# Revit family: MAD-412-I_Módulo analógico 2 salidas relé
name_source: partatom
category: Dispositivos de alarma de incendios
revit_build: Autodesk Revit 2017 (Build: 20190508_0315(x64)
units: mm (PartAtom-declared; Revit-internal decimal feet)

## family parameters
Anfitrión = Cara
Compartido = No
Corte con vacíos al cargar = No
Cota de conector redondo = Diámetro de uso
Mantener orientación de anotación = No
Punto de cálculo de habitación = No
Tipo de pieza = Normal

## types (1)
- MAD-412-I
    Altura = 100 mm
    Anchura = 100 mm
    Carga eléctrica = Otro
    Certificación = EN 54-18 y EN 54-17
    Comentarios de tipo = Los módulos son idóneos para la activación o paro de cualquier dispositivo. También son idóneos para interrelacionar sistemas donde las entradas de dichos sistemas admitan contactos libres de potencial, por ejemplo, el paro de la ventilación, el paro de los ascensores o la activación de los exutorios.
    Conexionado = 2 x 1,5 mm² trenzado y apantallado
    Consumo en alarma = < 3 mA
    Consumo en reposo = < 300 μA
    Cuerpo = ABS Rojo
    Código de montaje = PDETMAD-412-I
    Descripción = Módulo analógico de control con aislador incorporado de 2 salidas de relé libre de tensión que proporciona dos contactos C, NA, NC no reseteable. Marca Detnov, modelo MAD-412-I. Ocupa dos direcciones en el lazo. Alimentación directa desde el lazo. Incluye led indicador de estado. Conexionado mediante regletas extraíbles de hasta 2,5mm2 de sección. Posibilidad de ser instalado en carril DIN o montaje plano a pared en caja BOX-400. Consumo menor de 300μA en reposo. Color rojo. Dimensiones 100 x 82 x 23 mm. Certificado CPR EN54-18 y EN54-17.
    Elevación por defecto = 1219 mm
    Fabricante = Detnov Security
    Fases = 1
    Humedad relativa = 95% sin condensación
    Imagen de tipo = <Ninguno>
    Modelo = Módulo analógico MAD-412-I
    Potencia total = 0 VA
    Profundidad = 23 mm
    Teléfono = (+34) 93 371 60 25
    Temperatura trabajo = De -10ºC a 70ºC
    Tensión de trabajo = De 22 a 38VDC
    URL = https://www.detnov.com
    Voltaje = 230 V
    Índice IP = IP40
